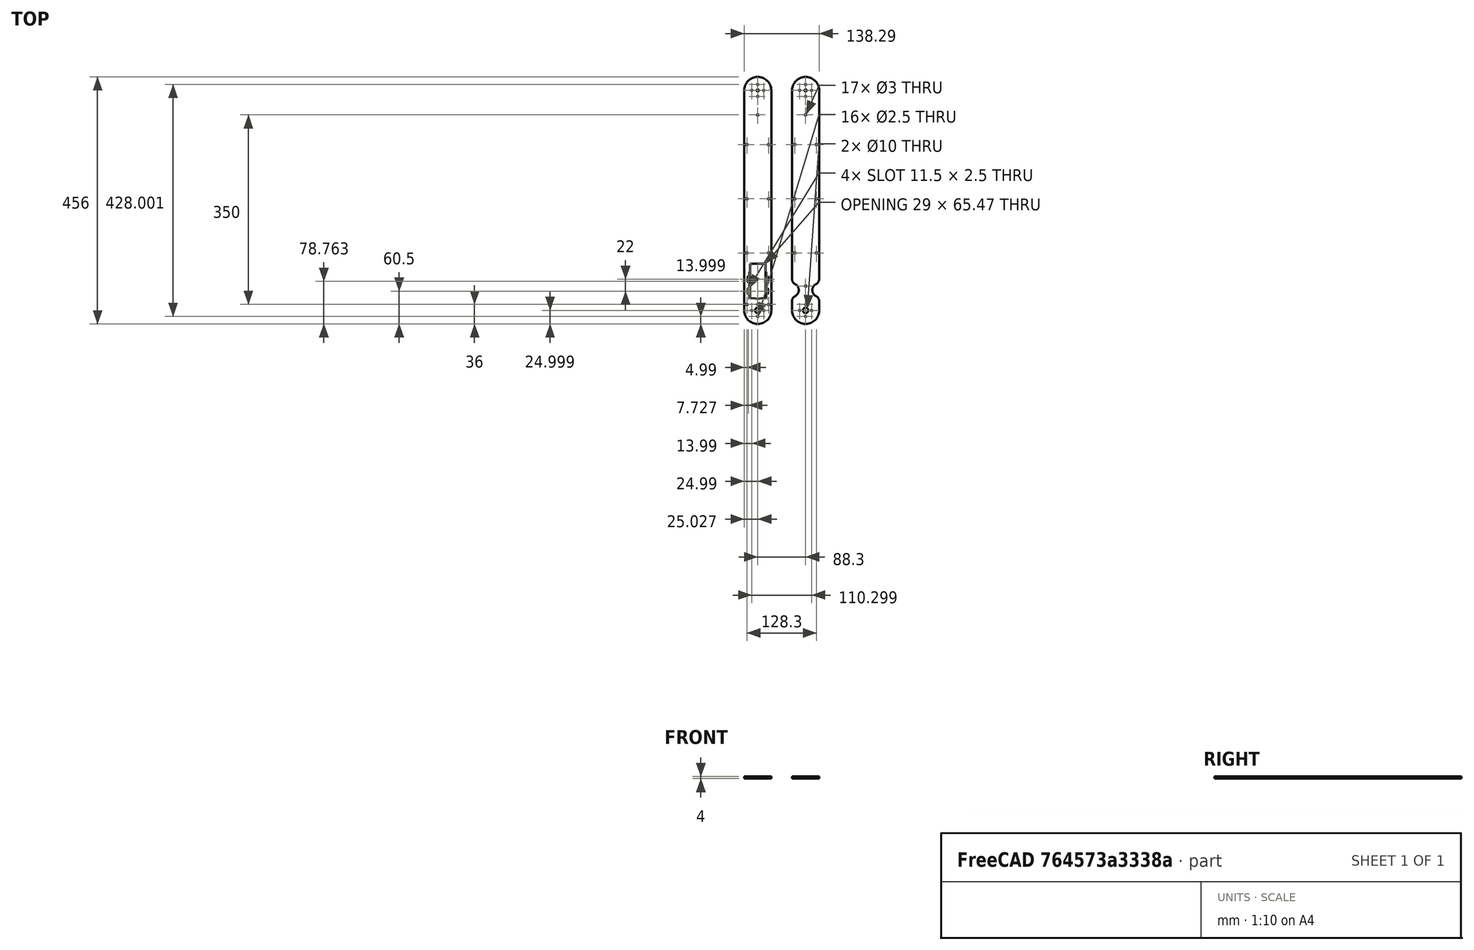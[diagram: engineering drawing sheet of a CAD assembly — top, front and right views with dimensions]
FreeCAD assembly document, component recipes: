
FREECAD ASSEMBLY — COMPONENT RECIPES ("arm_assembly_def3")

This assembly document has 2 components, labeled P0..P1 below (a component is one placed body or linked part). 2 of them carry a construction recipe — the FreeCAD feature program that regenerates the part from scratch, quoted from this document or its linked companion documents; the rest are supplied as boundary geometry only. No exploded tour is included for this assembly.
COMPONENT P0 — recipe-attached ("arm_low_1", modeled in this document).
Construction recipe (the document's own serialized feature program — sketch geometry with constraints, then the solid features built on it; lengths are millimeters unless a unit is written):

FEATURE [Sketcher::SketchObject] Sketch
  ArcFitTolerance = 1e-06
  AttachmentSupport = -> [XY_Plane]
  FullyConstrained = false
  MakeInternals = false
  MapMode = 5
  sketch-geometry (103):
    g0: LineSegment [constr] StartX=1.5008e-12 StartY=20 StartZ=0 EndX=1.5008e-12 EndY=-20 EndZ=0
    g1: LineSegment [constr] StartX=0 StartY=0 StartZ=0 EndX=0 EndY=400 EndZ=0
    g2: LineSegment [constr] StartX=1.5008e-12 StartY=20 StartZ=0 EndX=1.5008e-12 EndY=25 EndZ=0
    g3: Circle CenterX=0 CenterY=400 CenterZ=0 NormalX=0 NormalY=0 NormalZ=1 AngleXU=0 Radius=2
    g4: Circle CenterX=-10.9997 CenterY=400 CenterZ=0 NormalX=0 NormalY=0 NormalZ=1 AngleXU=0 Radius=1.25
    g5: Circle CenterX=0 CenterY=389 CenterZ=0 NormalX=0 NormalY=0 NormalZ=1 AngleXU=0 Radius=1.25
    g6: Circle CenterX=10.9997 CenterY=400 CenterZ=0 NormalX=0 NormalY=0 NormalZ=1 AngleXU=0 Radius=1.25
    g7: Circle CenterX=0 CenterY=411 CenterZ=0 NormalX=0 NormalY=0 NormalZ=1 AngleXU=0 Radius=1.25
    g8: LineSegment [constr] StartX=0 StartY=-5 StartZ=0 EndX=0 EndY=5.99996 EndZ=0
    g9: LineSegment [constr] StartX=0 StartY=0 StartZ=0 EndX=25.23 EndY=0 EndZ=0
    g10: LineSegment [constr] StartX=0 StartY=0 StartZ=0 EndX=-25 EndY=0 EndZ=0
    g11: LineSegment [constr] StartX=20.1368 StartY=86.1259 StartZ=0 EndX=20.1368 EndY=25.0259 EndZ=0
    g12: LineSegment [constr] StartX=0.036848 StartY=80.5 StartZ=0 EndX=14.5368 EndY=80.5 EndZ=0
    g13: LineSegment StartX=14.5368 StartY=80.5 StartZ=0 EndX=-14.4632 EndY=80.5 EndZ=0
    g14: LineSegment StartX=14.5368 StartY=80.5 StartZ=0 EndX=14.5368 EndY=25.0259 EndZ=0
    g15: Circle [constr] CenterX=17.3368 CenterY=78 CenterZ=0 NormalX=0 NormalY=0 NormalZ=1 AngleXU=0 Radius=1.25
    g16: LineSegment [constr] StartX=-20.0632 StartY=86.1259 StartZ=0 EndX=20.1368 EndY=86.1259 EndZ=0
    g17: Circle [constr] CenterX=17.3368 CenterY=56.0002 CenterZ=0 NormalX=0 NormalY=0 NormalZ=1 AngleXU=0 Radius=1.25
    g18: Circle [constr] CenterX=17.3368 CenterY=34 CenterZ=0 NormalX=0 NormalY=0 NormalZ=1 AngleXU=0 Radius=1.25
    g19: Circle [constr] CenterX=0.0368605 CenterY=38.0259 CenterZ=0 NormalX=0 NormalY=0 NormalZ=1 AngleXU=0 Radius=14
    g20: ArcOfCircle [constr] CenterX=0.0368605 CenterY=38.0259 CenterZ=0 NormalX=0 NormalY=0 NormalZ=1 AngleXU=0 Radius=14 StartAngle=4.33213 EndAngle=5.09264
    g21: LineSegment [constr] StartX=5.23308 StartY=25.0259 StartZ=0 EndX=14.5368 EndY=25.0259 EndZ=0
    g22: LineSegment [constr] StartX=14.5368 StartY=25.0259 StartZ=0 EndX=20.1368 EndY=25.0259 EndZ=0
    g23: LineSegment [constr] StartX=17.3368 StartY=56.0002 StartZ=0 EndX=-17.2632 EndY=56.0002 EndZ=0
    g24: LineSegment [constr] StartX=-20.0632 StartY=25.0259 StartZ=0 EndX=-20.0632 EndY=86.1259 EndZ=0
    g25: LineSegment StartX=-14.4632 StartY=80.5 StartZ=0 EndX=-14.4632 EndY=25.0259 EndZ=0
    g26: Circle [constr] CenterX=-17.2632 CenterY=78 CenterZ=0 NormalX=0 NormalY=0 NormalZ=1 AngleXU=0 Radius=1.25
    g27: Circle [constr] CenterX=-17.2632 CenterY=56.0002 CenterZ=0 NormalX=0 NormalY=0 NormalZ=1 AngleXU=0 Radius=1.25
    g28: Circle [constr] CenterX=-17.2632 CenterY=34 CenterZ=0 NormalX=0 NormalY=0 NormalZ=1 AngleXU=0 Radius=1.25
    g29: LineSegment [constr] StartX=-14.4632 StartY=25.0259 StartZ=0 EndX=-5.15937 EndY=25.0259 EndZ=0
    g30: LineSegment [constr] StartX=-20.0632 StartY=25.0259 StartZ=0 EndX=-14.4632 EndY=25.0259 EndZ=0
    g31: LineSegment [constr] StartX=25.23 StartY=199.98 StartZ=0 EndX=-25 EndY=199.98 EndZ=0
    g32: LineSegment [constr] StartX=25.23 StartY=199.98 StartZ=0 EndX=55.23 EndY=199.98 EndZ=0
    g33: LineSegment [constr] StartX=25.23 StartY=0 StartZ=0 EndX=55.23 EndY=0 EndZ=0
    g34: LineSegment [constr] StartX=55.23 StartY=0 StartZ=0 EndX=55.23 EndY=199.98 EndZ=0
    g35: LineSegment [constr] StartX=55.23 StartY=99.9898 StartZ=0 EndX=25.23 EndY=99.9898 EndZ=0
    g36: LineSegment [constr] StartX=25.23 StartY=99.9898 StartZ=0 EndX=-25 EndY=99.9898 EndZ=0
    g37: LineSegment [constr] StartX=25.23 StartY=399.959 StartZ=0 EndX=55.23 EndY=399.959 EndZ=0
    g38: LineSegment [constr] StartX=55.23 StartY=399.959 StartZ=0 EndX=55.23 EndY=199.98 EndZ=0
    g39: LineSegment [constr] StartX=55.23 StartY=299.969 StartZ=0 EndX=25.23 EndY=299.969 EndZ=0
    g40: LineSegment [constr] StartX=25.23 StartY=299.969 StartZ=0 EndX=-25 EndY=299.969 EndZ=0
    g41: LineSegment [constr] StartX=-25 StartY=299.969 StartZ=0 EndX=-20 EndY=299.969 EndZ=0
    g42: LineSegment [constr] StartX=-20 StartY=299.969 StartZ=0 EndX=-20 EndY=199.98 EndZ=0
    g43: LineSegment [constr] StartX=-20 StartY=199.98 StartZ=0 EndX=-20 EndY=99.9898 EndZ=0
    g44: LineSegment [constr] StartX=25.23 StartY=299.969 StartZ=0 EndX=20.23 EndY=299.969 EndZ=0
    g45: LineSegment [constr] StartX=20.23 StartY=299.969 StartZ=0 EndX=20.23 EndY=199.98 EndZ=0
    g46: LineSegment [constr] StartX=20.23 StartY=199.98 StartZ=0 EndX=20.23 EndY=99.9898 EndZ=0
    g47: Circle CenterX=-20 CenterY=299.969 CenterZ=0 NormalX=0 NormalY=0 NormalZ=1 AngleXU=0 Radius=1.5
    g48: Circle CenterX=20.23 CenterY=299.969 CenterZ=0 NormalX=0 NormalY=0 NormalZ=1 AngleXU=0 Radius=1.5
    g49: Circle CenterX=-20 CenterY=199.98 CenterZ=0 NormalX=0 NormalY=0 NormalZ=1 AngleXU=0 Radius=1.5
    g50: Circle CenterX=20.23 CenterY=199.98 CenterZ=0 NormalX=0 NormalY=0 NormalZ=1 AngleXU=0 Radius=1.5
    g51: Circle CenterX=-20 CenterY=99.9898 CenterZ=0 NormalX=0 NormalY=0 NormalZ=1 AngleXU=0 Radius=1.5
    g52: Circle CenterX=20.23 CenterY=99.9898 CenterZ=0 NormalX=0 NormalY=0 NormalZ=1 AngleXU=0 Radius=1.5
    g53: LineSegment [constr] StartX=-17.2632 StartY=34 StartZ=0 EndX=17.3368 EndY=34 EndZ=0
    g54: LineSegment [constr] StartX=-17.2632 StartY=34 StartZ=0 EndX=-17.2632 EndY=25 EndZ=0
    g55: LineSegment [constr] StartX=17.3368 StartY=34 StartZ=0 EndX=17.3368 EndY=25 EndZ=0
    g56: LineSegment [constr] StartX=-17.2632 StartY=78 StartZ=0 EndX=17.3368 EndY=78 EndZ=0
    g57: LineSegment [constr] StartX=-17.2632 StartY=78 StartZ=0 EndX=-17.2632 EndY=69 EndZ=0
    g58: LineSegment [constr] StartX=17.3368 StartY=78 StartZ=0 EndX=17.3368 EndY=69 EndZ=0
    g59: LineSegment StartX=-14.4632 StartY=25.0259 StartZ=0 EndX=-14.4632 EndY=22.0259 EndZ=0
    g60: LineSegment StartX=14.5368 StartY=25.0259 StartZ=0 EndX=14.5368 EndY=22.0259 EndZ=0
    g61: LineSegment [constr] StartX=-17.2632 StartY=56.0002 StartZ=0 EndX=-17.2632 EndY=47.0002 EndZ=0
    g62: LineSegment [constr] StartX=17.3368 StartY=56.0002 StartZ=0 EndX=17.3368 EndY=47.0002 EndZ=0
    g63: Circle [constr] CenterX=0.010165 CenterY=399.952 CenterZ=0 NormalX=0 NormalY=0 NormalZ=1 AngleXU=0 Radius=25.1076
    g64: LineSegment [constr] StartX=0 StartY=400 StartZ=0 EndX=0 EndY=374.844 EndZ=0
    g65: LineSegment [constr] StartX=0 StartY=374.844 StartZ=0 EndX=0 EndY=364.844 EndZ=0
    g66: Circle [constr] CenterX=0 CenterY=364.844 CenterZ=0 NormalX=0 NormalY=0 NormalZ=1 AngleXU=0 Radius=1.5
    g67: Circle [constr] CenterX=-17.2632 CenterY=69 CenterZ=0 NormalX=0 NormalY=0 NormalZ=1 AngleXU=0 Radius=1.25
    g68: Circle [constr] CenterX=17.3368 CenterY=69 CenterZ=0 NormalX=0 NormalY=0 NormalZ=1 AngleXU=0 Radius=1.25
    g69: ArcOfCircle CenterX=-17.2632 CenterY=56.0002 CenterZ=0 NormalX=0 NormalY=0 NormalZ=1 AngleXU=0 Radius=1.25 StartAngle=3.144e-13 EndAngle=3.14159
    g70: ArcOfCircle CenterX=-17.2632 CenterY=47.0002 CenterZ=0 NormalX=0 NormalY=0 NormalZ=1 AngleXU=0 Radius=1.25 StartAngle=3.14159 EndAngle=6.28319
    g71: LineSegment StartX=-16.0132 StartY=56.0002 StartZ=0 EndX=-16.0132 EndY=47.0002 EndZ=0
    g72: LineSegment StartX=-18.5132 StartY=56.0002 StartZ=0 EndX=-18.5132 EndY=47.0002 EndZ=0
    g73: ArcOfCircle CenterX=17.3368 CenterY=34 CenterZ=0 NormalX=0 NormalY=0 NormalZ=1 AngleXU=0 Radius=1.25 StartAngle=6e-16 EndAngle=3.14159
    g74: ArcOfCircle CenterX=17.3368 CenterY=25 CenterZ=0 NormalX=0 NormalY=0 NormalZ=1 AngleXU=0 Radius=1.25 StartAngle=3.14159 EndAngle=6.28319
    g75: LineSegment StartX=18.5868 StartY=34 StartZ=0 EndX=18.5868 EndY=25 EndZ=0
    g76: LineSegment StartX=16.0868 StartY=34 StartZ=0 EndX=16.0868 EndY=25 EndZ=0
    g77: LineSegment StartX=5.233 StartY=16.0259 StartZ=0 EndX=14.5368 EndY=16.0259 EndZ=0
    g78: ArcOfCircle CenterX=0.036848 CenterY=29.0259 CenterZ=0 NormalX=0 NormalY=0 NormalZ=1 AngleXU=0 Radius=14 StartAngle=4.33214 EndAngle=5.09264
    g79: LineSegment StartX=-5.15931 StartY=16.0259 StartZ=0 EndX=-14.4632 EndY=16.0259 EndZ=0
    g80: LineSegment StartX=-14.4632 StartY=22.0259 StartZ=0 EndX=-14.4632 EndY=16.0259 EndZ=0
    g81: LineSegment StartX=14.5368 StartY=22.0259 StartZ=0 EndX=14.5368 EndY=16.0259 EndZ=0
    g82: ArcOfCircle CenterX=17.3368 CenterY=56.0002 CenterZ=0 NormalX=0 NormalY=0 NormalZ=1 AngleXU=0 Radius=1.25 StartAngle=8.3e-15 EndAngle=3.14159
    g83: ArcOfCircle CenterX=17.3368 CenterY=47.0002 CenterZ=0 NormalX=0 NormalY=0 NormalZ=1 AngleXU=0 Radius=1.25 StartAngle=3.14159 EndAngle=6.28319
    g84: LineSegment StartX=18.5868 StartY=56.0002 StartZ=0 EndX=18.5868 EndY=47.0002 EndZ=0
    g85: LineSegment StartX=16.0868 StartY=56.0002 StartZ=0 EndX=16.0868 EndY=47.0002 EndZ=0
    g86: ArcOfCircle CenterX=-17.2632 CenterY=34 CenterZ=0 NormalX=0 NormalY=0 NormalZ=1 AngleXU=0 Radius=1.25 StartAngle=1e-16 EndAngle=3.14159
    g87: ArcOfCircle CenterX=-17.2632 CenterY=25 CenterZ=0 NormalX=0 NormalY=0 NormalZ=1 AngleXU=0 Radius=1.25 StartAngle=3.14159 EndAngle=6.28319
    g88: LineSegment StartX=-16.0132 StartY=34 StartZ=0 EndX=-16.0132 EndY=25 EndZ=0
    g89: LineSegment StartX=-18.5132 StartY=34 StartZ=0 EndX=-18.5132 EndY=25 EndZ=0
    g90: Circle [constr] CenterX=0 CenterY=-6 CenterZ=0 NormalX=0 NormalY=0 NormalZ=1 AngleXU=0 Radius=14
    g91: Circle [constr] CenterX=0.010165 CenterY=-5.99291 CenterZ=0 NormalX=0 NormalY=0 NormalZ=1 AngleXU=0 Radius=11
    g92: Circle CenterX=0 CenterY=-6 CenterZ=0 NormalX=0 NormalY=0 NormalZ=1 AngleXU=0 Radius=5
    g93: Circle CenterX=0 CenterY=-16.9997 CenterZ=0 NormalX=0 NormalY=0 NormalZ=1 AngleXU=0 Radius=1.25
    g94: Circle CenterX=10.9997 CenterY=-6 CenterZ=0 NormalX=0 NormalY=0 NormalZ=1 AngleXU=0 Radius=1.25
    g95: Circle CenterX=-10.9997 CenterY=-6 CenterZ=0 NormalX=0 NormalY=0 NormalZ=1 AngleXU=0 Radius=1.25
    g96: Circle CenterX=0 CenterY=4.99996 CenterZ=0 NormalX=0 NormalY=0 NormalZ=1 AngleXU=0 Radius=1.25
    g97: ArcOfCircle CenterX=0.010165 CenterY=-5.99291 CenterZ=0 NormalX=0 NormalY=0 NormalZ=1 AngleXU=0 Radius=25 StartAngle=3.14159 EndAngle=6.28319
    g98: ArcOfCircle CenterX=0.010165 CenterY=399.952 CenterZ=0 NormalX=0 NormalY=0 NormalZ=1 AngleXU=0 Radius=25 StartAngle=0 EndAngle=3.14159
    g99: LineSegment StartX=-24.9898 StartY=-5.99291 StartZ=0 EndX=-24.9898 EndY=399.952 EndZ=0
    g100: LineSegment StartX=25.0102 StartY=-5.99291 StartZ=0 EndX=25.0102 EndY=399.952 EndZ=0
    g101: LineSegment [constr] StartX=0 StartY=364.844 StartZ=0 EndX=0 EndY=354.844 EndZ=0
    g102: Circle CenterX=0 CenterY=354.844 CenterZ=0 NormalX=0 NormalY=0 NormalZ=1 AngleXU=0 Radius=1.5
  constraints (212):
    c: Vertical(g0)
    c: Vertical(g1)
    c: Coincident(g2,g0)
    c: Vertical(g2)
    c: Diameter(g3) = 4
    c: Coincident(g3,g1)
    c: Diameter(g7) = 2.5
    c: Diameter(g4) = 2.5
    c: Diameter(g5) = 2.5
    c: Diameter(g6) = 2.5
    c: Vertical(g8)
    c: Horizontal(g10)
    c: Horizontal(g9)
    c: Coincident(g16,g11)
    c: Coincident(g24,g16)
    c: Horizontal(g16)
    c: Vertical(g11)
    c: Vertical(g24)
    c: Distance(g11,g24) = 40.2
    c: Distance(g16,g24) = 61.1
    c: Diameter(g20) = 28
    c: Horizontal(g12)
    c: Coincident(g13,g12)
    c: Horizontal(g13)
    c: Coincident(g25,g13)
    c: Vertical(g25)
    c: Coincident(g14,g12)
    c: Vertical(g14)
    c: Coincident(g19,g20)
    c: PointOnObject(g20,g19)
    c: Coincident(g21,g20)
    c: Coincident(g21,g14)
    c: Horizontal(g21)
    c: Coincident(g22,g14)
    c: Coincident(g22,g11)
    c: Horizontal(g22)
    c: Coincident(g29,g25)
    c: Coincident(g29,g20)
    c: Horizontal(g29)
    c: Coincident(g30,g24)
    c: Coincident(g30,g25)
    c: Horizontal(g30)
    c: Coincident(g23,g17)
    c: Coincident(g23,g27)
    c: Horizontal(g23)
    c: DistanceY(g19,g1) = 361.974
    c: Horizontal(g31)
    c: Distance(g32) = 30
    c: Horizontal(g32)
    c: Coincident(g32,g31)
    c: Distance(g33) = 30
    c: Horizontal(g33)
    c: Coincident(g33,g9)
    c: PointOnObject(g33,g-1)
    c: Coincident(g34,g33)
    c: Coincident(g34,g32)
    c: Vertical(g34)
    c: Symmetric(g34,g34,g35)
    c: Horizontal(g35)
    c: Coincident(g36,g35)
    c: Horizontal(g36)
    c: Distance(g37) = 30
    c: Horizontal(g37)
    c: Coincident(g38,g37)
    c: Coincident(g38,g32)
    c: Symmetric(g38,g38,g39)
    c: Horizontal(g39)
    c: Coincident(g40,g39)
    c: Horizontal(g40)
    c: Distance(g41) = 5
    c: Coincident(g41,g40)
    c: PointOnObject(g41,g40)
    c: Coincident(g42,g41)
    c: PointOnObject(g42,g31)
    c: Vertical(g42)
    c: Coincident(g43,g42)
    c: PointOnObject(g43,g36)
    c: Vertical(g43)
    c: Distance(g44) = 5
    c: Coincident(g44,g39)
    c: PointOnObject(g44,g40)
    c: Coincident(g45,g44)
    c: PointOnObject(g45,g31)
    c: Vertical(g45)
    c: Coincident(g46,g45)
    c: PointOnObject(g46,g36)
    c: Vertical(g46)
    c: Coincident(g47,g41)
    c: Diameter(g47) = 3
    c: Coincident(g48,g44)
    c: Equal(g47,g48)
    c: Coincident(g49,g42)
    c: Equal(g47,g49)
    c: Coincident(g50,g45)
    c: Equal(g49,g50)
    c: Coincident(g51,g43)
    c: Equal(g49,g51)
    c: Coincident(g52,g46)
    c: Equal(g51,g52)
    c: Coincident(g53,g28)
    c: Coincident(g53,g18)
    c: Horizontal(g53)
    c: DistanceX(g53,g53) = 34.6
    c: Coincident(g54,g28)
    c: Vertical(g54)
    c: Coincident(g55,g18)
    c: Vertical(g55)
    c: Coincident(g56,g26)
    c: Coincident(g56,g15)
    c: Horizontal(g56)
    c: DistanceX(g56,g56) = 34.6
    c: Distance(g57) = 9
    c: Coincident(g57,g26)
    c: Vertical(g57)
    c: Coincident(g58,g15)
    c: Vertical(g58)
    c: DistanceX(g25,g14) = 29
    c: Distance(g59) = 3
    c: Coincident(g59,g25)
    c: Vertical(g59)
    c: Coincident(g60,g14)
    c: Vertical(g60)
    c: DistanceX(g23,g23) = 34.6
    c: Coincident(g61,g23)
    c: Vertical(g61)
    c: Coincident(g62,g17)
    c: Vertical(g62)
    c: DistanceX(g1) = 0
    c: DistanceY(g1) = 400
    c: Coincident(g64,g1)
    c: PointOnObject(g64,g63)
    c: Vertical(g64)
    c: Distance(g65) = 10
    c: Coincident(g65,g64)
    c: PointOnObject(g65,g1)
    c: Diameter(g66) = 3
    c: Coincident(g66,g65)
    c: DistanceX(g26) = -17.2632
    c: DistanceY(g26) = 78
    c: DistanceX(g23) = -17.2632
    c: DistanceY(g23) = 56.0002
    c: Equal(g58,g57)
    c: Equal(g61,g57)
    c: Equal(g62,g61)
    c: DistanceX(g28) = -17.2632
    c: DistanceY(g28) = 34
    c: Equal(g54,g61)
    c: Equal(g55,g54)
    c: Equal(g60,g59)
    c: Coincident(g67,g57)
    c: Equal(g67,g26)
    c: Coincident(g68,g58)
    c: Equal(g68,g15)
    c: Tangent(g69,g71) = 1.5708
    c: Tangent(g69,g72) = -1.5708
    c: Tangent(g70,g71) = 1.5708
    c: Tangent(g70,g72) = -1.5708
    c: Equal(g69,g70)
    c: Coincident(g69,g23)
    c: Coincident(g70,g61)
    c: Equal(g27,g69)
    c: Tangent(g73,g75) = 1.5708
    c: Tangent(g73,g76) = -1.5708
    c: Tangent(g74,g75) = 1.5708
    c: Tangent(g74,g76) = -1.5708
    c: Equal(g73,g74)
    c: Radius(g73) = 1.25
    c: Coincident(g73,g18)
    c: Coincident(g74,g55)
    c: Diameter(g78) = 28
    c: Coincident(g77,g78)
    c: Horizontal(g77)
    c: Coincident(g79,g78)
    c: Horizontal(g79)
    c: Coincident(g80,g59)
    c: Coincident(g80,g79)
    c: Vertical(g80)
    c: Coincident(g81,g60)
    c: Coincident(g81,g77)
    c: Vertical(g81)
    c: Tangent(g82,g84) = 1.5708
    c: Tangent(g82,g85) = -1.5708
    c: Tangent(g83,g84) = 1.5708
    c: Tangent(g83,g85) = -1.5708
    c: Equal(g82,g83)
    c: Tangent(g86,g88) = 1.5708
    c: Tangent(g86,g89) = -1.5708
    c: Tangent(g87,g88) = 1.5708
    c: Tangent(g87,g89) = -1.5708
    c: Equal(g86,g87)
    c: Diameter(g90) = 28
    c: Diameter(g91) = 22
    c: Diameter(g92) = 10
    c: Coincident(g92,g90)
    c: Diameter(g96) = 2.5
    c: Diameter(g95) = 2.5
    c: Diameter(g93) = 2.5
    c: Diameter(g94) = 2.5
    c: Tangent(g97,g99) = 1.5708
    c: Tangent(g97,g100) = -1.5708
    c: Tangent(g98,g99) = 1.5708
    c: Tangent(g98,g100) = -1.5708
    c: Equal(g97,g98)
    c: Vertical(g100)
    c: Radius(g97) = 25
    c: Coincident(g97,g91)
    c: Coincident(g98,g63)
    c: Distance(g101) = 10
    c: Coincident(g101,g65)
    c: PointOnObject(g101,g1)
    c: Coincident(g102,g101)
    c: Equal(g102,g66)
FEATURE [PartDesign::Pad] Pad
  Direction = (0,0,1)
  Length = 4
  Length2 = 10
  Profile = -> Sketch
  ReferenceAxis = -> Sketch [N_Axis]
  Refine = true
  Suppressed = false
  Type = 0
FEATURE [Sketcher::SketchObject] Sketch003
  ArcFitTolerance = 1e-06
  AttachmentSupport = -> [Pad]
  ExternalGeometry = -> [Pad]
  FullyConstrained = true
  MakeInternals = false
  MapMode = 5
  Placement = pos=(0,0,4) rot=(0,0,1;0rad)
  sketch-geometry (6):
    g0: LineSegment [constr] StartX=20.23 StartY=99.9898 StartZ=0 EndX=20.23 EndY=4.99996 EndZ=0
    g1: LineSegment [constr] StartX=0 StartY=4.99996 StartZ=0 EndX=20.23 EndY=4.99996 EndZ=0
    g2: Circle CenterX=20.23 CenterY=4.99996 CenterZ=0 NormalX=0 NormalY=0 NormalZ=1 AngleXU=0 Radius=1.5
    g3: LineSegment [constr] StartX=-20 StartY=99.9898 StartZ=0 EndX=-20 EndY=4.99996 EndZ=0
    g4: LineSegment [constr] StartX=0 StartY=4.99996 StartZ=0 EndX=-20 EndY=4.99996 EndZ=0
    g5: Circle CenterX=-20 CenterY=4.99996 CenterZ=0 NormalX=0 NormalY=0 NormalZ=1 AngleXU=0 Radius=1.5
  constraints (14):
    c: Coincident(g0,g-3)
    c: Vertical(g0)
    c: Coincident(g1,g-4)
    c: Horizontal(g1)
    c: Coincident(g1,g0)
    c: Coincident(g2,g0)
    c: Diameter(g2) = 3
    c: Coincident(g3,g-5)
    c: Vertical(g3)
    c: Coincident(g4,g1)
    c: Horizontal(g4)
    c: Coincident(g4,g3)
    c: Coincident(g5,g3)
    c: Equal(g5,g2)
FEATURE [PartDesign::Pocket] Pocket001
  BaseFeature = -> Pad
  Direction = (0,0,-1)
  Length = 12
  Length2 = 5
  Profile = -> Sketch003
  ReferenceAxis = -> Sketch003 [N_Axis]
  Refine = true
  Suppressed = false
  Type = 0
FEATURE [PartDesign::Body] Body  label="arm_low_1"
  AllowCompound = false
  Group = -> [Sketch,Pad,Sketch003,Pocket001]
  Origin = -> Origin
  Placement = pos=(-19.82,10,17.66) rot=(0,0,1;0rad)
  Tip = -> Pocket001
COMPONENT P1 — recipe-attached ("arm_high_1", modeled in this document).
Construction recipe (the document's own serialized feature program — sketch geometry with constraints, then the solid features built on it; lengths are millimeters unless a unit is written):

FEATURE [Sketcher::SketchObject] Sketch001
  ArcFitTolerance = 1e-06
  FullyConstrained = false
  MakeInternals = false
  MapMode = 5
  sketch-geometry (50):
    g0: Circle [constr] CenterX=0 CenterY=0.000303 CenterZ=0 NormalX=0 NormalY=0 NormalZ=1 AngleXU=0 Radius=14
    g1: Circle CenterX=0 CenterY=0.000303 CenterZ=0 NormalX=0 NormalY=0 NormalZ=1 AngleXU=0 Radius=2
    g2: Circle [constr] CenterX=0 CenterY=0 CenterZ=0 NormalX=0 NormalY=0 NormalZ=1 AngleXU=0 Radius=11
    g3: Circle CenterX=10.9997 CenterY=0.000303 CenterZ=0 NormalX=0 NormalY=0 NormalZ=1 AngleXU=0 Radius=1.25
    g4: Circle CenterX=0 CenterY=11 CenterZ=0 NormalX=0 NormalY=0 NormalZ=1 AngleXU=0 Radius=1.25
    g5: Circle CenterX=-10.9997 CenterY=0.000303 CenterZ=0 NormalX=0 NormalY=0 NormalZ=1 AngleXU=0 Radius=1.25
    g6: Circle CenterX=0 CenterY=-10.9994 CenterZ=0 NormalX=0 NormalY=0 NormalZ=1 AngleXU=0 Radius=1.25
    g7: LineSegment [constr] StartX=25 StartY=200 StartZ=0 EndX=-25 EndY=200 EndZ=0
    g8: LineSegment [constr] StartX=25 StartY=200 StartZ=0 EndX=55 EndY=200 EndZ=0
    g9: LineSegment [constr] StartX=25 StartY=0 StartZ=0 EndX=55 EndY=0 EndZ=0
    g10: LineSegment [constr] StartX=55 StartY=200 StartZ=0 EndX=55 EndY=0 EndZ=0
    g11: LineSegment [constr] StartX=55 StartY=100 StartZ=0 EndX=25 EndY=100 EndZ=0
    g12: LineSegment [constr] StartX=25 StartY=100 StartZ=0 EndX=-25 EndY=100 EndZ=0
    g13: LineSegment [constr] StartX=55 StartY=300 StartZ=0 EndX=25 EndY=300 EndZ=0
    g14: LineSegment [constr] StartX=25 StartY=300 StartZ=0 EndX=-25 EndY=300 EndZ=0
    g15: LineSegment [constr] StartX=-25 StartY=300 StartZ=0 EndX=-20 EndY=300 EndZ=0
    g16: LineSegment [constr] StartX=-20 StartY=300 StartZ=0 EndX=-20 EndY=200 EndZ=0
    g17: LineSegment [constr] StartX=-20 StartY=200 StartZ=0 EndX=-20 EndY=100 EndZ=0
    g18: LineSegment [constr] StartX=25 StartY=100 StartZ=0 EndX=20 EndY=100 EndZ=0
    g19: LineSegment [constr] StartX=20 StartY=100 StartZ=0 EndX=20 EndY=200 EndZ=0
    g20: LineSegment [constr] StartX=20 StartY=200 StartZ=0 EndX=20 EndY=300 EndZ=0
    g21: Circle CenterX=-20 CenterY=300 CenterZ=0 NormalX=0 NormalY=0 NormalZ=1 AngleXU=0 Radius=1.5
    g22: Circle CenterX=20 CenterY=300 CenterZ=0 NormalX=0 NormalY=0 NormalZ=1 AngleXU=0 Radius=1.5
    g23: Circle CenterX=-20 CenterY=200 CenterZ=0 NormalX=0 NormalY=0 NormalZ=1 AngleXU=0 Radius=1.5
    g24: Circle CenterX=20 CenterY=200 CenterZ=0 NormalX=0 NormalY=0 NormalZ=1 AngleXU=0 Radius=1.5
    g25: Circle CenterX=-20 CenterY=100 CenterZ=0 NormalX=0 NormalY=0 NormalZ=1 AngleXU=0 Radius=1.5
    g26: Circle CenterX=20 CenterY=100 CenterZ=0 NormalX=0 NormalY=0 NormalZ=1 AngleXU=0 Radius=1.5
    g27: Circle [constr] CenterX=0 CenterY=0 CenterZ=0 NormalX=0 NormalY=0 NormalZ=1 AngleXU=0 Radius=25
    g28: LineSegment [constr] StartX=0 StartY=0 StartZ=0 EndX=0 EndY=25 EndZ=0
    g29: LineSegment [constr] StartX=0 StartY=25 StartZ=0 EndX=0 EndY=35 EndZ=0
    g30: Circle [constr] CenterX=0 CenterY=35 CenterZ=0 NormalX=0 NormalY=0 NormalZ=1 AngleXU=0 Radius=1.5
    g31: LineSegment [constr] StartX=0 StartY=35 StartZ=0 EndX=0 EndY=45 EndZ=0
    g32: Circle CenterX=0 CenterY=45 CenterZ=0 NormalX=0 NormalY=0 NormalZ=1 AngleXU=0 Radius=1.5
    g33: Circle CenterX=0 CenterY=406.001 CenterZ=0 NormalX=0 NormalY=0 NormalZ=1 AngleXU=0 Radius=5
    g34: Circle CenterX=0 CenterY=417.001 CenterZ=0 NormalX=0 NormalY=0 NormalZ=1 AngleXU=0 Radius=1.25
    g35: Circle CenterX=-10.9997 CenterY=406.001 CenterZ=0 NormalX=0 NormalY=0 NormalZ=1 AngleXU=0 Radius=1.25
    g36: Circle CenterX=0 CenterY=395.001 CenterZ=0 NormalX=0 NormalY=0 NormalZ=1 AngleXU=0 Radius=1.25
    g37: LineSegment [constr] StartX=0 StartY=6.0003 StartZ=0 EndX=0 EndY=406.001 EndZ=0
    g38: Circle CenterX=10.9997 CenterY=406.001 CenterZ=0 NormalX=0 NormalY=0 NormalZ=1 AngleXU=0 Radius=1.25
    g39: LineSegment [constr] StartX=25 StartY=406.001 StartZ=0 EndX=55 EndY=406.001 EndZ=0
    g40: Circle [constr] CenterX=0 CenterY=406.001 CenterZ=0 NormalX=0 NormalY=0 NormalZ=1 AngleXU=0 Radius=25
    g41: LineSegment [constr] StartX=0 StartY=406.001 StartZ=0 EndX=0 EndY=381.001 EndZ=0
    g42: LineSegment [constr] StartX=0 StartY=381.001 StartZ=0 EndX=0 EndY=371.001 EndZ=0
    g43: Circle [constr] CenterX=0 CenterY=371.001 CenterZ=0 NormalX=0 NormalY=0 NormalZ=1 AngleXU=0 Radius=1.5
    g44: LineSegment [constr] StartX=0 StartY=371.001 StartZ=0 EndX=0 EndY=361.001 EndZ=0
    g45: Circle CenterX=0 CenterY=361.001 CenterZ=0 NormalX=0 NormalY=0 NormalZ=1 AngleXU=0 Radius=1.5
    g46: ArcOfCircle CenterX=0 CenterY=0 CenterZ=0 NormalX=0 NormalY=0 NormalZ=1 AngleXU=0 Radius=25 StartAngle=3.14159 EndAngle=6.28319
    g47: ArcOfCircle CenterX=0 CenterY=406.001 CenterZ=0 NormalX=0 NormalY=0 NormalZ=1 AngleXU=0 Radius=25 StartAngle=0 EndAngle=3.14159
    g48: LineSegment StartX=-25 StartY=6.97e-14 StartZ=0 EndX=-25 EndY=406.001 EndZ=0
    g49: LineSegment StartX=25 StartY=-6.1e-15 StartZ=0 EndX=25 EndY=406.001 EndZ=0
  constraints (91):
    c: Diameter(g0) = 28
    c: Diameter(g1) = 4
    c: Coincident(g1,g0)
    c: Diameter(g2) = 22
    c: Diameter(g4) = 2.5
    c: Diameter(g5) = 2.5
    c: Diameter(g6) = 2.5
    c: Diameter(g3) = 2.5
    c: Distance(g8) = 30
    c: Horizontal(g8)
    c: Coincident(g8,g7)
    c: Distance(g9) = 30
    c: Horizontal(g9)
    c: PointOnObject(g9,g-1)
    c: Coincident(g10,g8)
    c: Coincident(g10,g9)
    c: Symmetric(g10,g10,g11)
    c: Horizontal(g11)
    c: Coincident(g12,g11)
    c: Horizontal(g12)
    c: Horizontal(g13)
    c: Coincident(g14,g13)
    c: Horizontal(g14)
    c: Distance(g15) = 5
    c: Horizontal(g15)
    c: Coincident(g15,g14)
    c: Coincident(g16,g15)
    c: PointOnObject(g16,g7)
    c: Vertical(g16)
    c: Coincident(g17,g16)
    c: PointOnObject(g17,g12)
    c: Vertical(g17)
    c: Distance(g18) = 5
    c: Horizontal(g18)
    c: Coincident(g18,g11)
    c: Coincident(g19,g18)
    c: PointOnObject(g19,g7)
    c: Vertical(g19)
    c: Coincident(g20,g19)
    c: PointOnObject(g20,g14)
    c: Vertical(g20)
    c: Diameter(g21) = 3
    c: Coincident(g21,g15)
    c: Coincident(g22,g20)
    c: Equal(g21,g22)
    c: Coincident(g23,g16)
    c: Equal(g21,g23)
    c: Coincident(g24,g19)
    c: Equal(g23,g24)
    c: Coincident(g25,g17)
    c: Equal(g23,g25)
    c: Coincident(g26,g18)
    c: Equal(g25,g26)
    c: DistanceX(g2) = 0
    c: DistanceY(g2) = 0
    c: Coincident(g28,g2)
    c: PointOnObject(g28,g27)
    c: Vertical(g28)
    c: Distance(g29) = 10
    c: Coincident(g29,g28)
    c: Diameter(g30) = 3
    c: Coincident(g30,g29)
    c: Distance(g31) = 10
    c: Coincident(g31,g29)
    c: Coincident(g32,g31)
    c: Equal(g32,g30)
    c: Vertical(g37)
    c: Coincident(g33,g37)
    c: Diameter(g34) = 2.5
    c: Diameter(g35) = 2.5
    c: Diameter(g36) = 2.5
    c: Diameter(g38) = 2.5
    c: Horizontal(g39)
    c: Coincident(g40,g37)
    c: Coincident(g41,g37)
    c: PointOnObject(g41,g40)
    c: Vertical(g41)
    c: Coincident(g42,g41)
    c: PointOnObject(g42,g37)
    c: Coincident(g44,g42)
    c: Vertical(g44)
    c: Coincident(g45,g44)
    c: Tangent(g46,g48) = 1.5708
    c: Tangent(g46,g49) = -1.5708
    c: Tangent(g47,g48) = 1.5708
    c: Tangent(g47,g49) = -1.5708
    c: Equal(g46,g47)
    c: Vertical(g49)
    c: Radius(g46) = 25
    c: Coincident(g46,g27)
    c: Coincident(g47,g33)
FEATURE [PartDesign::Pad] Pad001
  Direction = (0,0,1)
  Length = 4
  Length2 = 10
  Profile = -> Sketch001
  ReferenceAxis = -> Sketch001 [N_Axis]
  Refine = true
  Suppressed = false
  Type = 0
FEATURE [Sketcher::SketchObject] Sketch002
  ArcFitTolerance = 1e-06
  AttachmentSupport = -> [Pad001]
  ExternalGeometry = -> [Pad001]
  FullyConstrained = true
  MakeInternals = false
  MapMode = 5
  Placement = pos=(0,0,4) rot=(0,0,1;0rad)
  sketch-geometry (7):
    g0: Circle [constr] CenterX=0 CenterY=406.001 CenterZ=0 NormalX=0 NormalY=0 NormalZ=1 AngleXU=0 Radius=45
    g1: LineSegment [constr] StartX=0 StartY=361.001 StartZ=0 EndX=25 EndY=361.001 EndZ=0
    g2: LineSegment [constr] StartX=25 StartY=361.001 StartZ=0 EndX=25 EndY=368.584 EndZ=0
    g3: LineSegment [constr] StartX=0 StartY=361.001 StartZ=0 EndX=-25 EndY=361.001 EndZ=0
    g4: LineSegment [constr] StartX=-25 StartY=361.001 StartZ=0 EndX=-25 EndY=368.584 EndZ=0
    g5: Circle CenterX=-25 CenterY=368.584 CenterZ=0 NormalX=0 NormalY=0 NormalZ=1 AngleXU=0 Radius=12.5
    g6: Circle CenterX=25 CenterY=368.584 CenterZ=0 NormalX=0 NormalY=0 NormalZ=1 AngleXU=0 Radius=12.5
  constraints (18):
    c: Coincident(g0,g-3)
    c: PointOnObject(g-4,g0)
    c: Coincident(g1,g-4)
    c: PointOnObject(g1,g-6)
    c: Horizontal(g1)
    c: Coincident(g2,g1)
    c: PointOnObject(g2,g0)
    c: Vertical(g2)
    c: Coincident(g3,g1)
    c: PointOnObject(g3,g-5)
    c: Horizontal(g3)
    c: Coincident(g4,g3)
    c: PointOnObject(g4,g0)
    c: Vertical(g4)
    c: Coincident(g5,g4)
    c: Diameter(g5) = 25
    c: Coincident(g6,g2)
    c: Equal(g6,g5)
FEATURE [PartDesign::Pocket] Pocket
  BaseFeature = -> Pad001
  Direction = (0,0,-1)
  Length = 11
  Length2 = 5
  Profile = -> Sketch002
  ReferenceAxis = -> Sketch002 [N_Axis]
  Refine = true
  Suppressed = false
  Type = 0
FEATURE [PartDesign::Fillet] Fillet
  Base = -> Pocket [Edge59,Edge9,Edge61,Edge6]
  BaseFeature = -> Pocket
  Radius = 10
  Refine = true
  SupportTransform = false
  Suppressed = false
  UseAllEdges = false
FEATURE [PartDesign::Body] Body001  label="arm_high_1"
  AllowCompound = false
  Group = -> [Sketch001,Pad001,Sketch002,Pocket,Fillet]
  Origin = -> Origin001
  Placement = pos=(68.48,410,17.66) rot=(0,0,1;3.14159rad)
  Tip = -> Fillet
PROVENANCE & LICENSES
A FreeCAD (.FCStd) document from a public repository crawl; recipes are the document's own serialized feature recipes (and, for linked parts, companion documents' recipes).
License: unknown-license-file.
